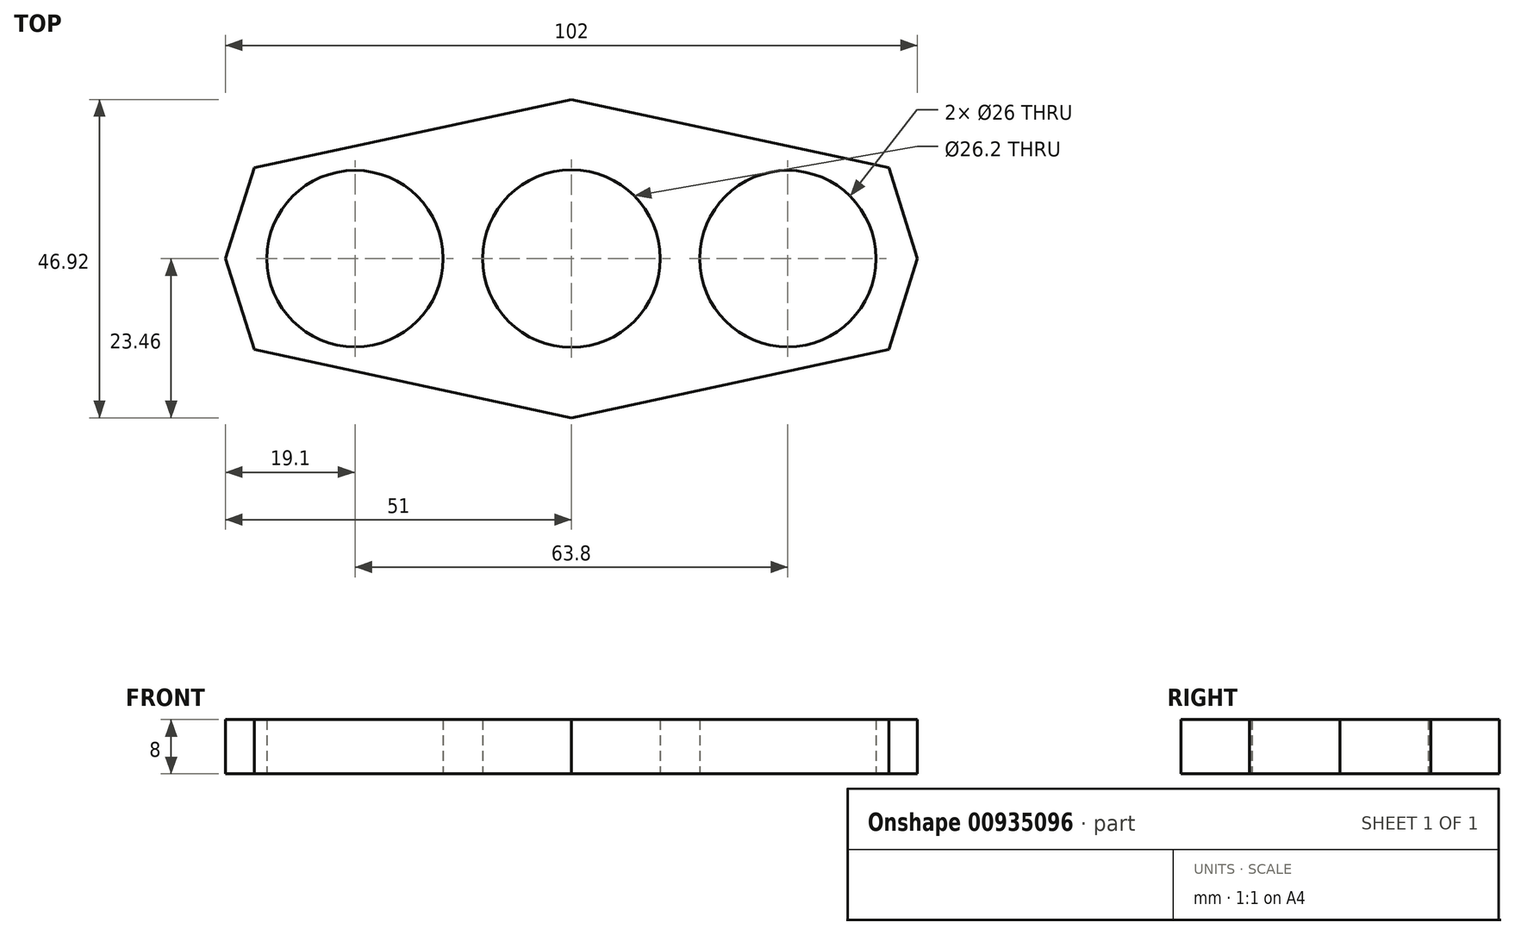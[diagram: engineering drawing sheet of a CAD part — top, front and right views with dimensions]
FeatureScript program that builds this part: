
annotation { "Feature Type Name" : "Feature", "Feature Type Description" : "" }
export const myFeature = defineFeature(function(context is Context, id is Id, definition is map)
    precondition{}
    {
        {
            var Q0;
            Q0=qCreatedBy(makeId("Top.planeOp"),FACE);
            var sketch = newSketch(context, id + "F0", { "sketchPlane" : qUnion([Q0])});
            skCircle(sketch, "E0", {"center": v(0, 0) * mm, "radius": 13.1 * mm});
            skCircle(sketch, "E1", {"center": v(31.9, 0) * mm, "radius": 13 * mm});
            skCircle(sketch, "E2", {"center": v(-31.9, 0) * mm, "radius": 13 * mm});
            skLineSegment(sketch, "E3", {"start": v(13.1, 0) * mm, "end": v(-44.9, 0) * mm, "construction": true});
            skLineSegment(sketch, "E4", {"start": v(-13.1, 0) * mm, "end": v(44.9, 0) * mm, "construction": true});
            skCircle(sketch, "E5", {"center": v(0, 0) * mm, "radius": 51 * mm, "construction": true});
            skLineSegment(sketch, "E6", {"start": v(-51, 0) * mm, "end": v(-46.77, -13.38) * mm});
            skLineSegment(sketch, "E7", {"start": v(-46.77, -13.38) * mm, "end": v(0, -23.46) * mm});
            skLineSegment(sketch, "E8", {"start": v(-51, 0) * mm, "end": v(-46.77, 13.38) * mm});
            skLineSegment(sketch, "E9", {"start": v(-46.77, 13.38) * mm, "end": v(0, 23.46) * mm});
            skLineSegment(sketch, "E10", {"start": v(0, 23.46) * mm, "end": v(46.77, 13.38) * mm});
            skLineSegment(sketch, "E11", {"start": v(46.77, 13.38) * mm, "end": v(51, 0) * mm});
            skLineSegment(sketch, "E12", {"start": v(51, 0) * mm, "end": v(46.77, -13.38) * mm});
            skLineSegment(sketch, "E13", {"start": v(46.77, -13.38) * mm, "end": v(0, -23.46) * mm});
            skSolve(sketch);
        }
        {
            var Q0;
            Q0 = qSketchRegion(id + "F0", true);
            extrude(context, id + "F1", {"entities" : qUnion([Q0]), "depth" : 8 * mm, "offsetDistance" : 25 * mm});
        }
    });
